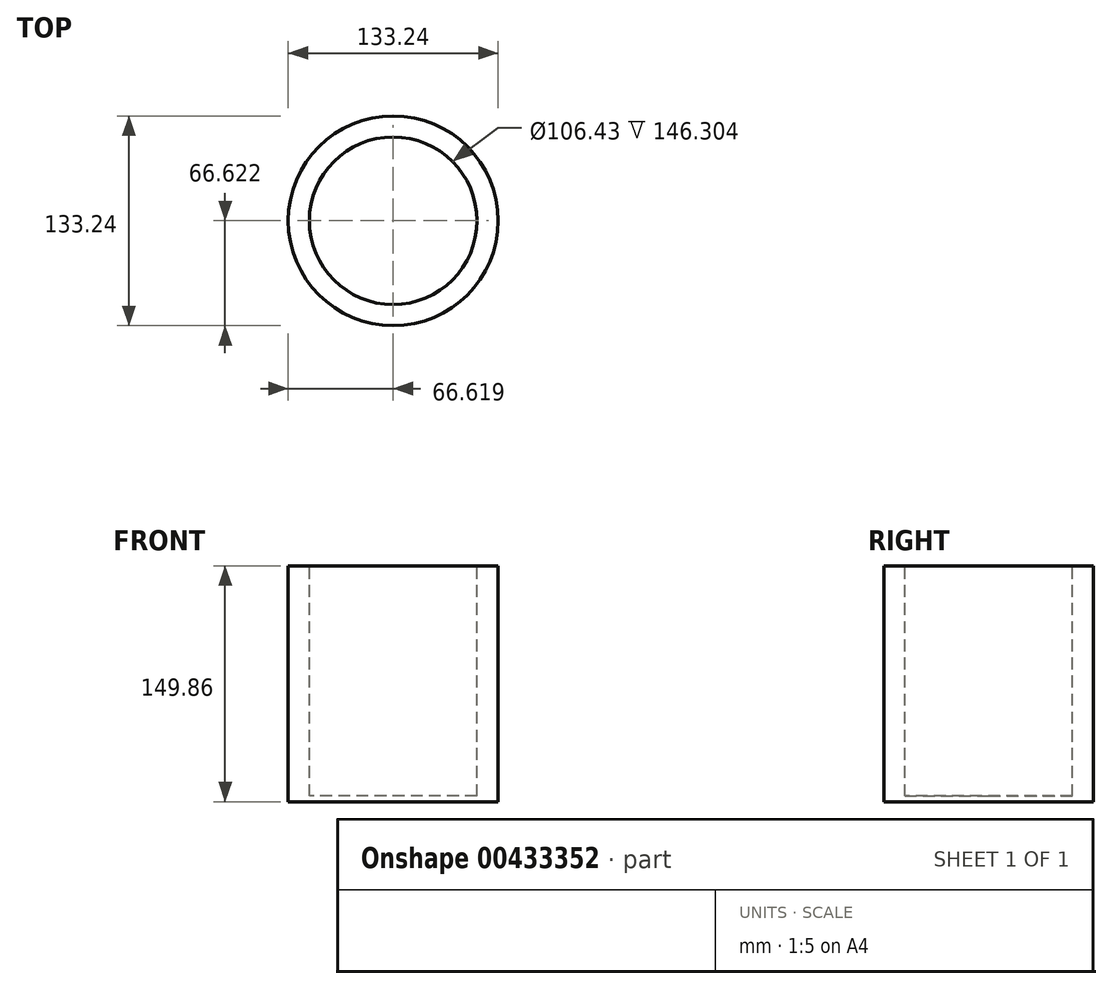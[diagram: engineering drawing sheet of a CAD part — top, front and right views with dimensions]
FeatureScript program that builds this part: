
annotation { "Feature Type Name" : "Feature", "Feature Type Description" : "" }
export const myFeature = defineFeature(function(context is Context, id is Id, definition is map)
    precondition{}
    {
        {
            var Q0;
            Q0=qCreatedBy(makeId("Top.planeOp"),FACE);
            var sketch = newSketch(context, id + "F0", { "sketchPlane" : qUnion([Q0])});
            skCircle(sketch, "E0", {"center": v(23.73, 29.58) * mm, "radius": 66.62 * mm});
            skSolve(sketch);
        }
        {
            var Q0;
            Q0=makeQuery(id+"F0.imprint","IMPRINT",FACE,{"disambiguationData":[TD([[makeQuery(id+"F0.imprint","IMPRINT",EDGE,{"derivedFrom":sQuery(id+"F0.wireOp",EDGE,"E0")}),1.0]])]});
            var Q1;
            Q1=sQuery(id+"F0.wireOp",EDGE,"E0");
            extrude(context, id + "F1", {"entities" : qUnion([Q0]), "surfaceEntities" : qUnion([Q1]), "depth" : 149.86 * mm});
        }
        {
            var Q0;
            Q0=makeQuery(id+"F1.opExtrude","CAP_FACE",FACE,{"disambiguationData":[OSD([sQuery(id+"F0.wireOp",EDGE,"E0")])],"isStart":false});
            var sketch = newSketch(context, id + "F2", { "sketchPlane" : qUnion([Q0])});
            skCircle(sketch, "E1", {"center": v(23.73, 29.58) * mm, "radius": 53.21 * mm});
            skSolve(sketch);
        }
        {
            var Q0;
            Q0=makeQuery(id+"F2.imprint","IMPRINT",FACE,{"disambiguationData":[TD([[makeQuery(id+"F2.imprint","IMPRINT",EDGE,{"derivedFrom":sQuery(id+"F2.wireOp",EDGE,"E1")}),1.0]])]});
            extrude(context, id + "F3", {"entities" : qUnion([Q0]), "operationType" : NewBodyOperationType.REMOVE, "oppositeDirection" : true, "depth" : 146.3 * mm});
        }
    });
